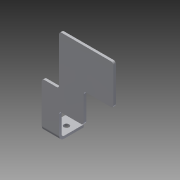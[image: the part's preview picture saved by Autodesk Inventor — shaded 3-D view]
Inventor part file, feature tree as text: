
AUTODESK INVENTOR PART (.ipt)
format: ipt  version: 2013 (Build 170138000, 138)  size: 201,216 bytes
history: native  units: in
note: dims shown in document units (in); Inventor stores cm internally (conversion verified against a paired STEP export)
features: sketch x5, sheet_metal_op x4, other x4, extrude x2, fillet x1, reference x1
ambient origin geometry x8: Origin, YZ Plane, XZ Plane, XY Plane, X Axis, Y Axis, Z Axis, Center Point
bodies: Solid1 (feature_tree)
feature tree (17):
  sheet_metal_op  "Face1"
  sheet_metal_op  "Flange1"
  extrude  "Extrusion1"  Depth=0.125in
  extrude  "Extrusion2"  Depth=0.25in
  fillet  "Fillet2"  Radius=0.125in
  sketch  "Sketch1"  dims[d0=0.125in d1=0.125in]
  other  "Plate1"
  sketch  "Sketch2"  dims[d2=0.0625in d3=0.25in d4=0.125in]
  other  "Plate2"
  sheet_metal_op  "Bend1"
  sheet_metal_op  "Corner1"
  sketch  "Sketch3"  dims[d5=1.25in d6=90.0deg d7=0.125in]
  reference  "Reference1"
  sketch  "Sketch5"  dims[d8=0.5in]
  sketch  "Sketch6"  dims[d9=0.125in d10=0.125in d11=0.125in d12=0.0in d13=1.5in d14=1.5in d15=0.0in d17=0.5in d18=0.0in d19=0.125in]
  other  "Cut1"
  other  "Definition1"
